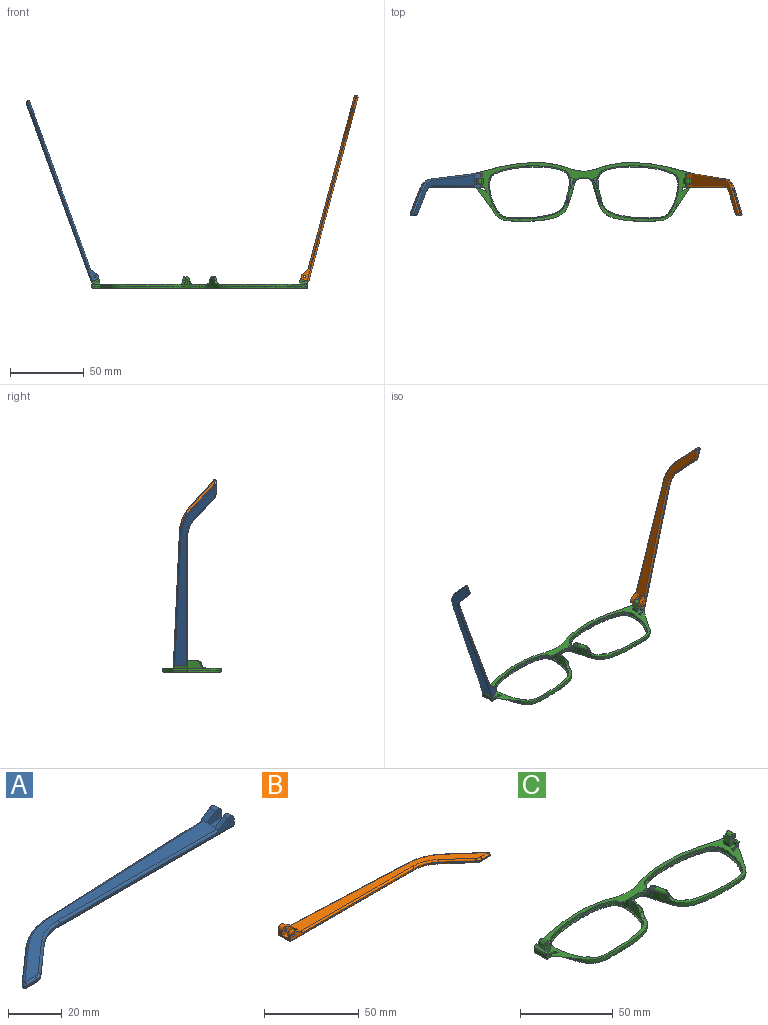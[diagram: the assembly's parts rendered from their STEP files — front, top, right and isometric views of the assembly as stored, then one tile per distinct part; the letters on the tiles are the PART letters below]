
ASSEMBLY  parts=3 mates=2
PART A: 43 faces, bbox 130.2x29.5x5.9 mm
  f0: plane 9.62x3.72mm, normal (1,0,0), area 24.7mm2, adj f1,f3,f4,f5,f10,f16,f18,f28
  f1: cylinder r=2.2mm len=3.45mm, axis (0,-1,0), area 11mm2, adj f0,f2,f4,f37
  f2: plane 6.01x3.91mm, normal (-0.55,0,0.84), area 12.7mm2, adj f1,f4,f9,f19,f37
  f3: plane 2.26x0.1mm, normal (0,0,1), area 0.1mm2, adj f0,f5,f18
  f4: plane 92.1x4.9mm, normal (0,-1,0), area 79.9mm2, adj f0,f1,f2,f14,f19,f36,f42
  f5: plane 93.42x4.13mm, normal (-0.04,1,0), area 64.8mm2, adj f0,f3,f11,f15,f17,f27,f28
  f6: plane 17.82x15.72mm, normal (-0.66,0.75,0), area 14.3mm2, adj f11,f12,f25,f30
  f7: plane 5.46x0.6mm, normal (0,-1,0), area 3.3mm2, adj f12,f13,f23,f32
  f8: plane 14.99x13.23mm, normal (0.66,-0.75,0), area 12mm2, adj f13,f14,f21,f34
  f9: plane 121.18x26.73mm, normal (0,0,1), area 627.7mm2, adj f2,f17,f19,f20,f21,f22,f23,f25
  f10: plane 129.1x27.08mm, normal (0,0,-1), area 686.5mm2, adj f0,f28,f29,f30,f32,f33,f34,f35
  f11: cylinder r=30mm len=18.52mm, axis (0,0,-1), area 12.2mm2, adj f5,f6,f26,f29
  f12: cylinder r=1mm len=1.75mm, axis (0,0,-1), area 1.5mm2, adj f6,f7,f24,f31
  f13: cylinder r=5mm len=3.31mm, axis (0,0,-1), area 2.2mm2, adj f7,f8,f22,f33
  f14: cylinder r=20mm len=13.23mm, axis (0,0,1), area 8.7mm2, adj f4,f8,f20,f35
  f15: plane 5.66x0.25mm, normal (0,0,-1), area 0.7mm2, adj f5,f17,f18
  f16: cylinder r=2.2mm len=3.45mm, axis (0,-1,0), area 14.8mm2, adj f0,f17,f18,f38
  f17: plane 6.01x3.91mm, normal (-0.55,0,0.84), area 16.9mm2, adj f5,f9,f15,f16,f18,f27,f38
  f18: plane 7.92x3.3mm, normal (0,1,0), area 15.9mm2, adj f0,f3,f15,f16,f17,f41
  f19: cylinder r=1mm len=84.18mm, axis (-1,0,0), area 131.4mm2, adj f2,f4,f9,f20
  f20: torus R=21mm, axis (0,0,1), area 23.1mm2, adj f9,f14,f19,f21
  f21: cylinder r=1mm len=15.65mm, axis (-0.75,-0.66,0), area 31.4mm2, adj f8,f9,f20,f22
  f22: torus R=4mm, axis (0,0,1), area 5.3mm2, adj f9,f13,f21,f23
  f23: cylinder r=1mm len=5.46mm, axis (-1,0,0), area 8.6mm2, adj f7,f9,f22,f24
  f24: sphere r=1mm, area 2.4mm2, adj f12,f23,f25
  f25: cylinder r=1mm len=18.48mm, axis (0.75,0.66,0), area 37.3mm2, adj f6,f9,f24,f26
  f26: torus R=29mm, axis (0,0,1), area 31.6mm2, adj f9,f11,f25,f27
  f27: cylinder r=1mm len=85.5mm, axis (1,0.04,0), area 133.5mm2, adj f5,f9,f17,f26
  f28: cylinder r=1mm len=93.46mm, axis (-1,-0.04,0), area 146.9mm2, adj f0,f5,f10,f29
  f29: torus R=29mm, axis (0,0,1), area 31.6mm2, adj f10,f11,f28,f30
  f30: cylinder r=1mm len=18.48mm, axis (-0.75,-0.66,0), area 37.3mm2, adj f6,f10,f29,f31
  f31: sphere r=1mm, area 2.4mm2, adj f12,f30,f32
  f32: cylinder r=1mm len=5.46mm, axis (1,0,0), area 8.6mm2, adj f7,f10,f31,f33
  f33: torus R=4mm, axis (0,0,1), area 5.3mm2, adj f10,f13,f32,f34
  f34: cylinder r=1mm len=15.65mm, axis (0.75,0.66,0), area 31.4mm2, adj f8,f10,f33,f35
  f35: torus R=21mm, axis (0,0,1), area 23.1mm2, adj f10,f14,f34,f36
  f36: cylinder r=1mm len=92.1mm, axis (1,0,0), area 144.7mm2, adj f0,f4,f10,f35
  f37: plane 7.92x4.7mm, normal (0,1,0), area 27mm2, adj f0,f1,f2,f39,f40,f42
  f38: plane 7.92x4.7mm, normal (0,-1,0), area 27mm2, adj f0,f16,f17,f39,f40,f41
  f39: plane 7.92x4.1mm, normal (0,0,1), area 32.5mm2, adj f0,f37,f38,f40
  f40: plane 4.1x1.4mm, normal (1,0,0), area 5.7mm2, adj f9,f37,f38,f39
  f41: cylinder r=0.5mm len=3.1mm, axis (0,-1,0), area 9.7mm2, adj f18,f38
  f42: cylinder r=0.5mm len=2.3mm, axis (0,-1,0), area 7.2mm2, adj f4,f37
PART B: 43 faces, bbox 130.2x29.5x5.9 mm
  f0: plane 9.62x3.72mm, normal (-1,0,0), area 24.7mm2, adj f1,f3,f4,f5,f10,f16,f18,f28
  f1: cylinder r=2.2mm len=3.45mm, axis (0,-1,0), area 11mm2, adj f0,f2,f4,f37
  f2: plane 6.01x3.91mm, normal (0.55,0,0.84), area 12.7mm2, adj f1,f4,f9,f19,f37
  f3: plane 2.26x0.1mm, normal (0,0,1), area 0.1mm2, adj f0,f5,f18
  f4: plane 92.1x4.9mm, normal (0,-1,0), area 78.2mm2, adj f0,f1,f2,f14,f19,f36,f42
  f5: plane 93.42x4.13mm, normal (0.04,1,0), area 64.8mm2, adj f0,f3,f11,f15,f17,f27,f28
  f6: plane 17.82x15.72mm, normal (0.66,0.75,0), area 14.3mm2, adj f11,f12,f25,f30
  f7: plane 5.46x0.6mm, normal (0,-1,0), area 3.3mm2, adj f12,f13,f23,f32
  f8: plane 14.99x13.23mm, normal (-0.66,-0.75,0), area 12mm2, adj f13,f14,f21,f34
  f9: plane 121.18x26.73mm, normal (0,0,1), area 627.7mm2, adj f2,f17,f19,f20,f21,f22,f23,f25
  f10: plane 129.1x27.08mm, normal (0,0,-1), area 686.5mm2, adj f0,f28,f29,f30,f32,f33,f34,f35
  f11: cylinder r=30mm len=18.52mm, axis (0,0,-1), area 12.2mm2, adj f5,f6,f26,f29
  f12: cylinder r=1mm len=1.75mm, axis (0,0,-1), area 1.5mm2, adj f6,f7,f24,f31
  f13: cylinder r=5mm len=3.31mm, axis (0,0,-1), area 2.2mm2, adj f7,f8,f22,f33
  f14: cylinder r=20mm len=13.23mm, axis (0,0,1), area 8.7mm2, adj f4,f8,f20,f35
  f15: plane 5.66x0.25mm, normal (0,0,-1), area 0.7mm2, adj f5,f17,f18
  f16: cylinder r=2.2mm len=3.45mm, axis (0,-1,0), area 14.8mm2, adj f0,f17,f18,f38
  f17: plane 6.01x3.91mm, normal (0.55,0,0.84), area 16.9mm2, adj f5,f9,f15,f16,f18,f27,f38
  f18: plane 7.92x3.3mm, normal (0,1,0), area 14.3mm2, adj f0,f3,f15,f16,f17,f41
  f19: cylinder r=1mm len=84.18mm, axis (1,0,0), area 131.4mm2, adj f2,f4,f9,f20
  f20: torus R=21mm, axis (0,0,1), area 23.1mm2, adj f9,f14,f19,f21
  f21: cylinder r=1mm len=15.65mm, axis (0.75,-0.66,0), area 31.4mm2, adj f8,f9,f20,f22
  f22: torus R=4mm, axis (0,0,1), area 5.3mm2, adj f9,f13,f21,f23
  f23: cylinder r=1mm len=5.46mm, axis (1,0,0), area 8.6mm2, adj f7,f9,f22,f24
  f24: sphere r=1mm, area 2.4mm2, adj f12,f23,f25
  f25: cylinder r=1mm len=18.48mm, axis (-0.75,0.66,0), area 37.3mm2, adj f6,f9,f24,f26
  f26: torus R=29mm, axis (0,0,1), area 31.6mm2, adj f9,f11,f25,f27
  f27: cylinder r=1mm len=85.5mm, axis (-1,0.04,0), area 133.5mm2, adj f5,f9,f17,f26
  f28: cylinder r=1mm len=93.46mm, axis (1,-0.04,0), area 146.9mm2, adj f0,f5,f10,f29
  f29: torus R=29mm, axis (0,0,1), area 31.6mm2, adj f10,f11,f28,f30
  f30: cylinder r=1mm len=18.48mm, axis (0.75,-0.66,0), area 37.3mm2, adj f6,f10,f29,f31
  f31: sphere r=1mm, area 2.4mm2, adj f12,f30,f32
  f32: cylinder r=1mm len=5.46mm, axis (-1,0,0), area 8.6mm2, adj f7,f10,f31,f33
  f33: torus R=4mm, axis (0,0,1), area 5.3mm2, adj f10,f13,f32,f34
  f34: cylinder r=1mm len=15.65mm, axis (-0.75,0.66,0), area 31.4mm2, adj f8,f10,f33,f35
  f35: torus R=21mm, axis (0,0,1), area 23.1mm2, adj f10,f14,f34,f36
  f36: cylinder r=1mm len=92.1mm, axis (-1,0,0), area 144.7mm2, adj f0,f4,f10,f35
  f37: plane 7.92x4.7mm, normal (0,1,0), area 25.4mm2, adj f0,f1,f2,f39,f40,f42
  f38: plane 7.92x4.7mm, normal (0,-1,0), area 25.4mm2, adj f0,f16,f17,f39,f40,f41
  f39: plane 7.92x4.1mm, normal (0,0,1), area 32.5mm2, adj f0,f37,f38,f40
  f40: plane 4.1x1.4mm, normal (-1,0,0), area 5.7mm2, adj f9,f37,f38,f39
  f41: cylinder r=0.88mm len=3.1mm, axis (0,-1,0), area 17mm2, adj f18,f38
  f42: cylinder r=0.88mm len=2.3mm, axis (0,-1,0), area 12.6mm2, adj f4,f37
PART C: 118 faces, bbox 148.1x40.9x18 mm
  f0: bspline ~1.82x1.22mm, area 0.7mm2, adj f2,f7,f37,f52
  f1: plane 147.73x40.5mm, normal (0,0,1), area 772.9mm2, adj f4,f5,f6,f7,f8,f12,f20,f23
  f2: bspline ~5.39x4.93mm, area 12.7mm2, adj f0,f7,f37,f41,f43,f52,f53
  f3: plane 4.46x1.45mm, normal (0,0,1), area 0.1mm2, adj f7,f38
  f4: plane 1.23x0.04mm, normal (0,0,1), area 0mm2, adj f1,f7,f22
  f5: plane 6.97x5.07mm, normal (0,1,0), area 22.7mm2, adj f1,f20,f21,f25,f27,f28,f30,f31
  f6: plane 3.2x2.36mm, normal (0,-1,0), area 5.7mm2, adj f1,f20,f26,f29
  f7: extruded ~73.26x39.84mm, area 292.7mm2, adj f0,f1,f2,f3,f4,f8,f13,f14
  f8: extruded ~35.39x5.69mm, area 72.2mm2, adj f1,f7,f18,f67
  f9: plane 144.78x37.85mm, normal (0,0,-1), area 478.1mm2, adj f13,f15,f17,f18,f19,f71,f73,f75
  f10: plane 56.31x36.53mm, normal (0,0,1), area 124.8mm2, adj f11,f19
  f11: extruded ~55.63x36.1mm, area 160.7mm2, adj f10,f12
  f12: extruded ~55.63x36.1mm, area 220.4mm2, adj f1,f11,f39,f40,f41,f42,f43,f44
  f13: bspline ~73.27x30.39mm, area 161.7mm2, adj f7,f9,f14,f71
  f14: bspline ~1x1mm, area 0.8mm2, adj f7,f13,f15
  f15: bspline ~8.99x1.23mm, area 12.6mm2, adj f7,f9,f14,f16
  f16: bspline ~1.04x1mm, area 0.7mm2, adj f7,f15,f17
  f17: bspline ~45.86x8.59mm, area 59.8mm2, adj f7,f9,f16,f18
  f18: bspline ~37.01x6.7mm, area 56.6mm2, adj f8,f9,f17,f76
  f19: bspline ~56.15x36.68mm, area 237.6mm2, adj f9,f10
  f20: plane 4x2.36mm, normal (-1,0,0), area 9.5mm2, adj f1,f5,f6,f21
  f21: plane 4x0.02mm, normal (0.34,0,0.94), area 0.1mm2, adj f5,f20,f28
  f22: plane 2.76x2.53mm, normal (0,-1,0), area 3.9mm2, adj f4,f26,f27,f35,f56
  f23: plane 7.67x1.6mm, normal (0.94,0,-0.34), area 13mm2, adj f1,f35,f36,f56
  f24: plane 2.1x1.69mm, normal (0,1,0), area 2.8mm2, adj f1,f25,f27,f36,f56
  f25: plane 3.3x2.1mm, normal (-1,0,0), area 6.9mm2, adj f1,f5,f24,f27
  f26: plane 2.35x2.1mm, normal (-1,0,0), area 4.9mm2, adj f1,f6,f22,f27,f29
  f27: plane 9.65x1.24mm, normal (0,0,1), area 8.2mm2, adj f5,f22,f24,f25,f26,f29,f30,f56
  f28: plane 4x3.31mm, normal (-0.94,0,0.34), area 14.1mm2, adj f5,f21,f29,f32
  f29: plane 5.77x5.06mm, normal (0,-1,0), area 17mm2, adj f6,f26,f27,f28,f30,f31,f32,f33
  f30: plane 4x2.21mm, normal (0.94,0,-0.34), area 9.4mm2, adj f5,f27,f29,f33
  f31: plane 4x0.01mm, normal (0.34,0,0.94), area 0mm2, adj f5,f29,f32,f33
  f32: cylinder r=1.98mm len=4mm, axis (0,1,0), area 12.4mm2, adj f5,f28,f29,f31
  f33: cylinder r=1.98mm len=4mm, axis (0,-1,0), area 12.4mm2, adj f5,f29,f30,f31
  f34: cylinder r=0.88mm len=4mm, axis (0,-1,0), area 22mm2, adj f5,f29
  f35: cone r=1mm half-angle=20deg, axis (0,0,1), area 2.3mm2, adj f1,f22,f23,f56
  f36: cylinder r=1mm len=2.28mm, axis (-0.34,0,-0.94), area 3mm2, adj f1,f23,f24,f56
  f37: extruded ~3.67x3.11mm, area 5.9mm2, adj f0,f2,f7,f59
  f38: extruded ~4.44x3.32mm, area 15.1mm2, adj f3,f7,f42,f43,f55
  f39: extruded ~4.98x1.36mm, area 6.6mm2, adj f12,f41
  f40: plane 3.63x0.97mm, normal (0,0,1), area 0.3mm2, adj f12,f41,f43
  f41: bspline ~15.5x15.35mm, area 6.4mm2, adj f2,f12,f39,f40,f54
  f42: bspline ~7.26x7.26mm, area 6.3mm2, adj f12,f38,f43,f55
  f43: bspline ~10.29x4.84mm, area 21.4mm2, adj f2,f7,f12,f38,f40,f42
  f44: plane 2.88x1.51mm, normal (0,0,-1), area 1.8mm2, adj f12,f45
  f45: cylinder r=2.28mm len=2.86mm, axis (0,0,1), area 1.8mm2, adj f1,f12,f44,f54
  f46: plane 2.5x1.83mm, normal (0,0,-1), area 1.7mm2, adj f12,f47
  f47: cylinder r=2.28mm len=2.47mm, axis (0,0,1), area 1.7mm2, adj f1,f12,f46
  f48: plane 1.79x1.31mm, normal (0,0,-1), area 0.9mm2, adj f12,f49
  f49: cylinder r=1.3mm len=1.78mm, axis (0,0,1), area 1.3mm2, adj f1,f12,f48
  f50: plane 1.95x1.68mm, normal (0,0,-1), area 1.5mm2, adj f12,f51
  f51: cylinder r=1.3mm len=1.93mm, axis (0,0,1), area 1.5mm2, adj f1,f12,f50
  f52: bspline ~2.66x2.04mm, area 1.9mm2, adj f0,f2,f7,f53,f58
  f53: bspline ~3.55x3.47mm, area 3.7mm2, adj f1,f2,f52,f54,f58
  f54: bspline ~5.1x3.97mm, area 7.6mm2, adj f1,f12,f41,f45,f53
  f55: bspline ~3.7x3.66mm, area 7.8mm2, adj f1,f7,f12,f38,f42
  f56: plane 9.71x1.44mm, normal (0.34,0,0.94), area 13.9mm2, adj f22,f23,f24,f27,f35,f36
  f57: bspline ~6.38x2.14mm, area 2.6mm2, adj f1,f7,f58,f115
  f58: bspline ~2.1x1.46mm, area 0.6mm2, adj f7,f52,f53,f57
  f59: bspline ~5.24x1.75mm, area 0mm2, adj f7,f37
  f60: bspline ~2.19x1.4mm, area 0.7mm2, adj f61,f66,f95,f110
  f61: bspline ~6.1x4.93mm, area 12.6mm2, adj f60,f66,f95,f99,f101,f110,f111
  f62: plane 4.46x1.45mm, normal (0,0,1), area 0.1mm2, adj f66,f96
  f63: plane 1.23x0.04mm, normal (0,0,1), area 0mm2, adj f1,f66,f80
  f64: plane 6.97x5.07mm, normal (0,1,0), area 22.7mm2, adj f1,f78,f79,f83,f85,f86,f88,f89
  f65: plane 3.2x2.36mm, normal (0,-1,0), area 5.7mm2, adj f1,f78,f84,f87
  f66: extruded ~73.26x39.84mm, area 292.7mm2, adj f1,f7,f60,f61,f62,f63,f67,f71
  f67: extruded ~35.39x5.69mm, area 72.2mm2, adj f1,f8,f66,f76
  f68: plane 56.31x36.53mm, normal (0,0,1), area 124.8mm2, adj f69,f77
  f69: extruded ~55.63x36.1mm, area 160.7mm2, adj f68,f70
  f70: extruded ~55.63x36.1mm, area 220.4mm2, adj f1,f69,f97,f98,f99,f100,f101,f102
  f71: bspline ~73.83x30.39mm, area 161.7mm2, adj f9,f13,f66,f72
  f72: bspline ~1x1mm, area 0.8mm2, adj f66,f71,f73
  f73: bspline ~8.99x1.23mm, area 12.6mm2, adj f9,f66,f72,f74
  f74: bspline ~1.04x1mm, area 0.8mm2, adj f66,f73,f75
  f75: bspline ~45.86x8.59mm, area 59.8mm2, adj f9,f66,f74,f76
  f76: bspline ~37.01x6.7mm, area 56.6mm2, adj f9,f18,f67,f75
  f77: bspline ~56.15x36.68mm, area 237.6mm2, adj f9,f68
  f78: plane 4x2.36mm, normal (1,0,0), area 9.5mm2, adj f1,f64,f65,f79
  f79: plane 4x0.02mm, normal (-0.34,0,0.94), area 0.1mm2, adj f64,f78,f86
  f80: plane 2.76x2.53mm, normal (0,-1,0), area 3.9mm2, adj f63,f84,f85,f93,f114
  f81: plane 7.67x1.6mm, normal (-0.94,0,-0.34), area 13mm2, adj f1,f93,f94,f114
  f82: plane 2.1x1.69mm, normal (0,1,0), area 2.8mm2, adj f1,f83,f85,f94,f114
  f83: plane 3.3x2.1mm, normal (1,0,0), area 6.9mm2, adj f1,f64,f82,f85
  f84: plane 2.35x2.1mm, normal (1,0,0), area 4.9mm2, adj f1,f65,f80,f85,f87
  f85: plane 9.65x1.24mm, normal (0,0,1), area 8.2mm2, adj f64,f80,f82,f83,f84,f87,f88,f114
  f86: plane 4x3.31mm, normal (0.94,0,0.34), area 14.1mm2, adj f64,f79,f87,f90
  f87: plane 5.77x5.06mm, normal (0,-1,0), area 17mm2, adj f65,f84,f85,f86,f88,f89,f90,f91
  f88: plane 4x2.21mm, normal (-0.94,0,-0.34), area 9.4mm2, adj f64,f85,f87,f91
  f89: plane 4x0.01mm, normal (-0.34,0,0.94), area 0mm2, adj f64,f87,f90,f91
  f90: cylinder r=1.98mm len=4mm, axis (0,1,0), area 12.4mm2, adj f64,f86,f87,f89
  f91: cylinder r=1.98mm len=4mm, axis (0,-1,0), area 12.4mm2, adj f64,f87,f88,f89
  f92: cylinder r=0.88mm len=4mm, axis (0,-1,0), area 22mm2, adj f64,f87
  f93: cone r=1mm half-angle=20deg, axis (0,0,1), area 2.3mm2, adj f1,f80,f81,f114
  f94: cylinder r=1mm len=2.28mm, axis (0.34,0,-0.94), area 3mm2, adj f1,f81,f82,f114
  f95: extruded ~3.67x3.11mm, area 5.9mm2, adj f60,f61,f66,f117
  f96: extruded ~4.44x3.32mm, area 15.1mm2, adj f62,f66,f100,f101,f113
  f97: extruded ~4.98x1.36mm, area 6.6mm2, adj f70,f99
  f98: plane 3.63x0.97mm, normal (0,0,1), area 0.3mm2, adj f70,f99,f101
  f99: bspline ~15.5x15.35mm, area 6.4mm2, adj f61,f70,f97,f98,f112
  f100: bspline ~7.26x7.26mm, area 6.2mm2, adj f70,f96,f101,f113
  f101: bspline ~10.29x4.84mm, area 21.5mm2, adj f61,f66,f70,f96,f98,f100
  f102: plane 2.88x1.51mm, normal (0,0,-1), area 1.8mm2, adj f70,f103
  f103: cylinder r=2.28mm len=2.86mm, axis (0,0,1), area 1.8mm2, adj f1,f70,f102,f112
  f104: plane 2.5x1.83mm, normal (0,0,-1), area 1.7mm2, adj f70,f105
  f105: cylinder r=2.28mm len=2.47mm, axis (0,0,1), area 1.7mm2, adj f1,f70,f104
  f106: plane 1.79x1.31mm, normal (0,0,-1), area 0.9mm2, adj f70,f107
  f107: cylinder r=1.3mm len=1.78mm, axis (0,0,1), area 1.3mm2, adj f1,f70,f106
  f108: plane 1.95x1.68mm, normal (0,0,-1), area 1.5mm2, adj f70,f109
  f109: cylinder r=1.3mm len=1.93mm, axis (0,0,1), area 1.5mm2, adj f1,f70,f108
  f110: bspline ~2.65x2.03mm, area 1.9mm2, adj f60,f61,f66,f111,f116
  f111: bspline ~3.55x3.47mm, area 3.7mm2, adj f1,f61,f110,f112,f116
  f112: bspline ~4.88x3.94mm, area 7.6mm2, adj f1,f70,f99,f103,f111
  f113: bspline ~3.7x3.66mm, area 7.8mm2, adj f1,f66,f70,f96,f100
  f114: plane 9.71x1.44mm, normal (-0.34,0,0.94), area 13.9mm2, adj f80,f81,f82,f85,f93,f94
  f115: bspline ~6.38x2.14mm, area 2.6mm2, adj f1,f57,f66,f116
  f116: bspline ~2.1x1.46mm, area 0.6mm2, adj f66,f110,f111,f115
  f117: bspline ~5.24x1.75mm, area 0mm2, adj f66,f95
PLACE A rot(axis=(0,1,0),70deg) t=(-93.64,-8.56,59.47)mm
PLACE B rot(axis=(0,-1,0),75deg) t=(59.33,-8.56,-58.14)mm
PLACE C t=(1.28,-3.95,-2.31)mm
MATE revolute A.f1 <-> C.f90  axis (0,-1,0) through (-69.76,-0.1,4.68)mm
MATE revolute B.f41 <-> C.f33  axis (0,-1,0) through (72.33,-0.1,4.68)mm
